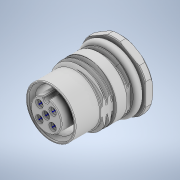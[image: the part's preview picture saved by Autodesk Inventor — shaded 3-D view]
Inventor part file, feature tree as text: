
AUTODESK INVENTOR PART (.ipt)
format: ipt  version: 2021 (Build 250183000, 183)  size: 815,104 bytes
history: native  units: mm
features: sketch x2, other x1, extrude x1, projected_geometry x1, imported_body x1
ambient origin geometry x8: Origin, YZ Plane, XZ Plane, XY Plane, X Axis, Y Axis, Z Axis, Center Point
bodies: Solid1 (feature_tree)
feature tree (6):
  other  "Repaired Geometry1"
  extrude  "Extrusion1"  [1 undecoded]
  sketch  "3D Sketch1"
  sketch  "Sketch2"  dims[d0=10.0mm d1=0.0mm]
  projected_geometry  "Projected Loop1"
  imported_body  "Base1"
note: 1 required parameter value undecoded (feature->parameter linkage not recoverable at this tier; creation-order binding heuristic only, values carry confidence <= 0.55)
